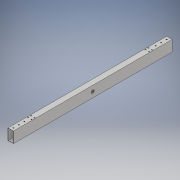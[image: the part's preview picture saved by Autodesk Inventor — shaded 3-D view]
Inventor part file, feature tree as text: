
AUTODESK INVENTOR PART (.ipt)
format: ipt  version: 2018 (Build 220112000, 112)  size: 165,376 bytes
history: native  units: in
note: dims shown in document units (in); Inventor stores cm internally (conversion verified against a paired STEP export)
features: extrude x4, sketch x4
ambient origin geometry x8: Origin, YZ Plane, XZ Plane, XY Plane, X Axis, Y Axis, Z Axis, Center Point
bodies: Solid1 (feature_tree)
feature tree (8):
  extrude  "Extrusion1"  Depth=2.0in
  extrude  "Extrusion4"  Depth=29.0in TaperAngle=0.0deg
  extrude  "Extrusion5"  Depth=1.0in
  extrude  "Extrusion6"  Depth=1.0in
  sketch  "Sketch1"  dims[d0=1.0in d1=2.0in]
  sketch  "Sketch4"  dims[d2=0.0625in d3=29.0in d4=0.0in]
  sketch  "Sketch5"  dims[d15=0.5in d16=1.0in]
  sketch  "Sketch6"  dims[d17=1.0in d18=0.2031in d19=6.0in d20=0.0in d21=1.0in d22=0.59in d23=1.0in d24=0.0in d26=3.5in d28=0.187in d29=0.6299in d30=0.5315in d31=0.1811in d33=14.5in d34=10.9375in d35=0.0in]
